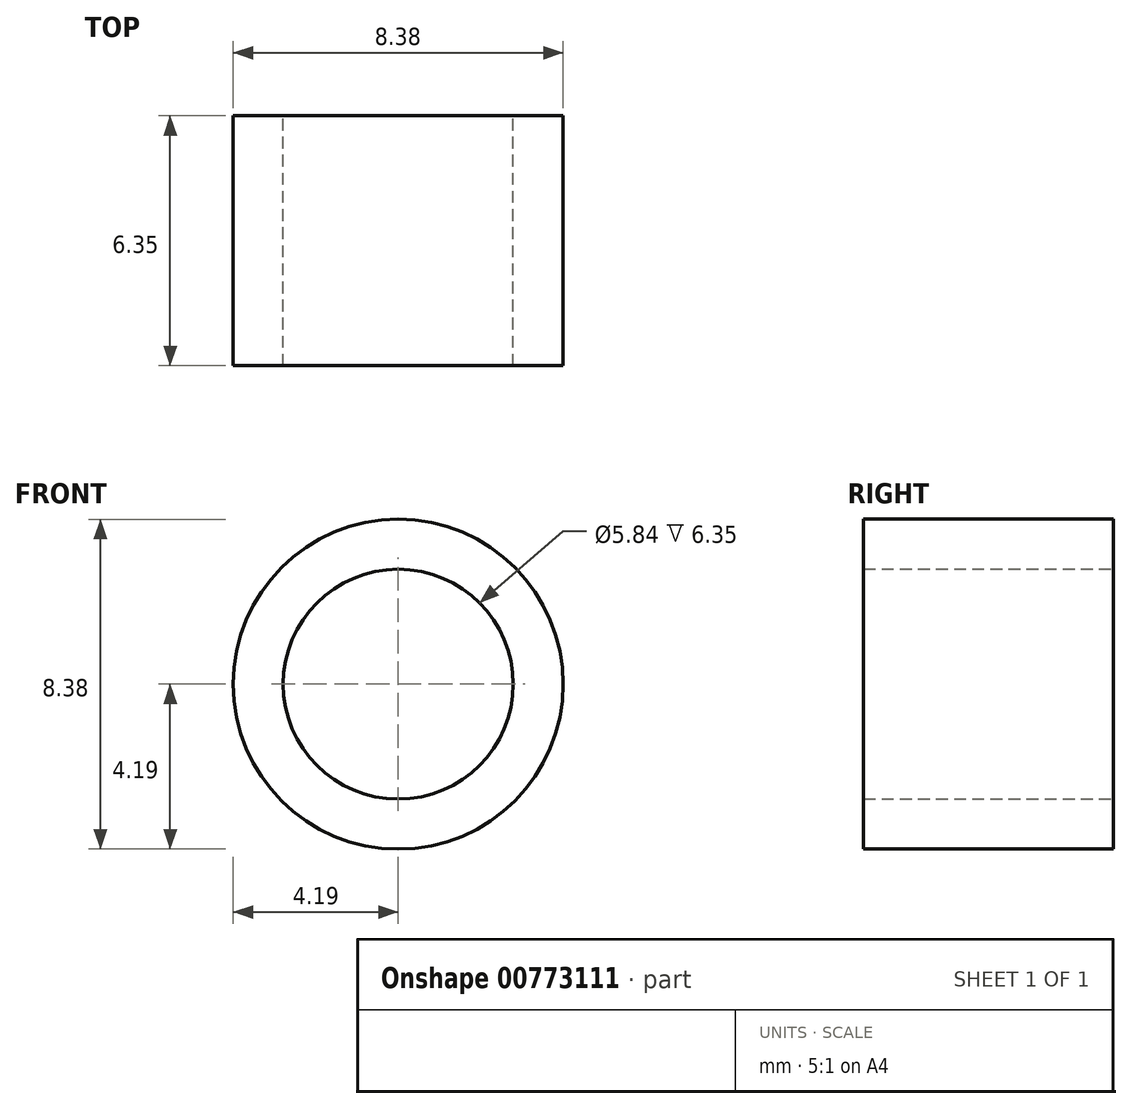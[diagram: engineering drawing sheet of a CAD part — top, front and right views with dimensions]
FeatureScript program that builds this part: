
annotation { "Feature Type Name" : "Feature", "Feature Type Description" : "" }
export const myFeature = defineFeature(function(context is Context, id is Id, definition is map)
    precondition{}
    {
        {
            var Q0;
            Q0=qCreatedBy(makeId("Front.planeOp"),FACE);
            var sketch = newSketch(context, id + "F0", { "sketchPlane" : qUnion([Q0])});
            skCircle(sketch, "E0", {"center": v(0, 0) * mm, "radius": 2.92 * mm});
            skCircle(sketch, "E1", {"center": v(0, 0) * mm, "radius": 4.2 * mm});
            skCircle(sketch, "E2", {"center": v(0, 0) * mm, "radius": 8.26 * mm, "construction": true});
            skCircle(sketch, "E3", {"center": v(16.51, 0) * mm, "radius": 8.26 * mm, "construction": true});
            skCircle(sketch, "E4.1.0", {"center": v(8.26, 14.3) * mm, "radius": 8.26 * mm, "construction": true});
            skCircle(sketch, "E4.2.0", {"center": v(-8.25, 14.3) * mm, "radius": 8.26 * mm, "construction": true});
            skCircle(sketch, "E4.3.0", {"center": v(-16.51, 0) * mm, "radius": 8.26 * mm, "construction": true});
            skCircle(sketch, "E4.4.0", {"center": v(-8.26, -14.3) * mm, "radius": 8.26 * mm, "construction": true});
            skCircle(sketch, "E4.5.0", {"center": v(8.26, -14.3) * mm, "radius": 8.26 * mm, "construction": true});
            skCircle(sketch, "E5", {"center": v(24.84, 14.34) * mm, "radius": 8.33 * mm, "construction": true});
            skCircle(sketch, "E6.1.0", {"center": v(0, 28.68) * mm, "radius": 8.33 * mm, "construction": true});
            skCircle(sketch, "E6.2.0", {"center": v(-24.84, 14.34) * mm, "radius": 8.33 * mm, "construction": true});
            skCircle(sketch, "E6.3.0", {"center": v(-24.84, -14.34) * mm, "radius": 8.33 * mm, "construction": true});
            skCircle(sketch, "E6.4.0", {"center": v(0, -28.68) * mm, "radius": 8.33 * mm, "construction": true});
            skCircle(sketch, "E6.5.0", {"center": v(24.84, -14.34) * mm, "radius": 8.33 * mm, "construction": true});
            skSolve(sketch);
        }
        {
            var Q0;
            Q0 = qSketchRegion(id + "F0", true);
            extrude(context, id + "F1", {"entities" : qUnion([Q0]), "depth" : 6.35 * mm, "offsetDistance" : 25.4 * mm});
        }
    });
